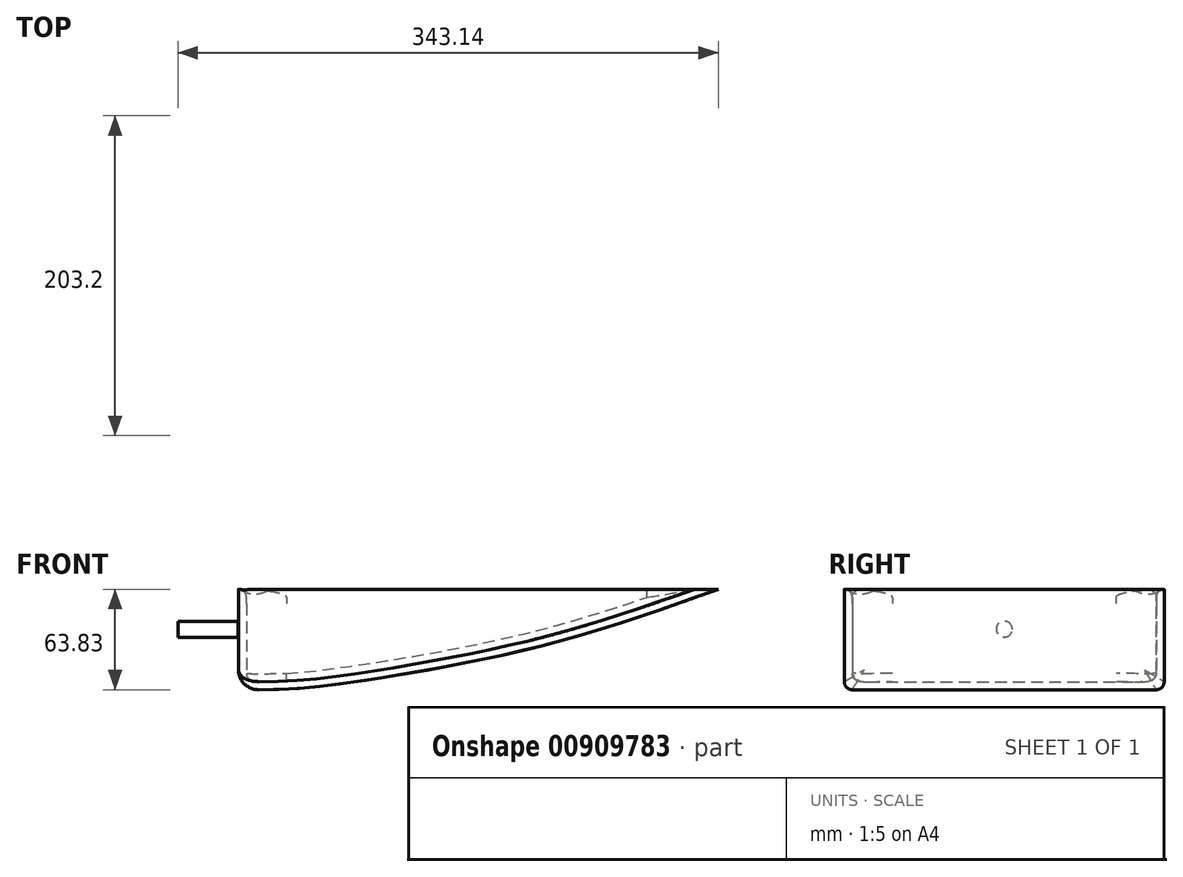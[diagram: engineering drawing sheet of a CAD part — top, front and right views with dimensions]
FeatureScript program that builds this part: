
annotation { "Feature Type Name" : "Feature", "Feature Type Description" : "" }
export const myFeature = defineFeature(function(context is Context, id is Id, definition is map)
    precondition{}
    {
        {
            var Q0;
            Q0=qCreatedBy(makeId("Front.planeOp"),FACE);
            var sketch = newSketch(context, id + "F0", { "sketchPlane" : qUnion([Q0])});
            skLineSegment(sketch, "E0", {"start": v(-126.76, 0) * mm, "end": v(178.04, 0) * mm});
            skLineSegment(sketch, "E1", {"start": v(-126.76, 0) * mm, "end": v(-126.76, -63.5) * mm});
            skFitSpline(sketch, "E2", {"points": [v(-126.76, -63.5) * mm, v(-96.17, -63.5) * mm, v(-41.35, -57.1) * mm, v(69.17, -35.07) * mm, v(178.04, 0) * mm], "startDerivative": vector(180.45, -5.15) * mm, "endDerivative": vector(339.41, 120.82) * mm});
            skSolve(sketch);
        }
        {
            var Q0;
            Q0 = qSketchRegion(id + "F0", true);
            extrude(context, id + "F1", {"entities" : qUnion([Q0]), "depth" : 203.2 * mm, "offsetDistance" : 25.4 * mm});
        }
        {
            var Q0;
            Q0=makeQuery(id+"F1.opExtrude","SWEPT_FACE",FACE,{"disambiguationData":[OSD([sQuery(id+"F0.wireOp",EDGE,"E0")])]});
            shell(context, id + "F2", {"entities" : qUnion([Q0]), "thickness" : 5.08 * mm});
        }
        {
            var Q0;
            {var subQ0=sQuery(id+"F0.wireOp",EDGE,"E2");Q0=makeQuery(id+"F2.opShell","OFFSET_EDGE",EDGE,{"disambiguationData":[OSD([subQ0]),TDD([makeQuery(id+"F1.opExtrude","CAP_EDGE",EDGE,{"disambiguationData":[OSD([subQ0])],"isStart":false})])]});}
            var Q1;
            {var subQ0=sQuery(id+"F0.wireOp",EDGE,"E2");Q1=makeQuery(id+"F2.opShell","OFFSET_EDGE",EDGE,{"disambiguationData":[OSD([subQ0]),TDD([makeQuery(id+"F1.opExtrude","CAP_EDGE",EDGE,{"disambiguationData":[OSD([subQ0])],"isStart":true})])]});}
            var Q2;
            Q2=makeQuery(id+"F1.opExtrude","CAP_EDGE",EDGE,{"disambiguationData":[OSD([sQuery(id+"F0.wireOp",EDGE,"E2")])],"isStart":true});
            var Q3;
            Q3=makeQuery(id+"F1.opExtrude","CAP_EDGE",EDGE,{"disambiguationData":[OSD([sQuery(id+"F0.wireOp",EDGE,"E2")])],"isStart":false});
            var Q4;
            {var subQ0=sQuery(id+"F0.wireOp",EDGE,"E0");Q4=makeQuery(id+"F2.opShell","OFFSET_EDGE",EDGE,{"disambiguationData":[OSD([subQ0]),TDD([makeQuery(id+"F1.opExtrude","CAP_EDGE",EDGE,{"disambiguationData":[OSD([subQ0])],"isStart":false})])]});}
            var Q5;
            Q5=makeQuery(id+"F2.opShell","OFFSET_EDGE",EDGE,{"disambiguationData":[OSD([sQuery(id+"F0.wireOp",EDGE,"E0"),sQuery(id+"F0.wireOp",EDGE,"E1")])]});
            var Q6;
            {var subQ0=sQuery(id+"F0.wireOp",EDGE,"E0");Q6=makeQuery(id+"F2.opShell","OFFSET_EDGE",EDGE,{"disambiguationData":[OSD([subQ0]),TDD([makeQuery(id+"F1.opExtrude","CAP_EDGE",EDGE,{"disambiguationData":[OSD([subQ0])],"isStart":true})])]});}
            var Q7;
            Q7=makeQuery(id+"F2.opShell","OFFSET_EDGE",EDGE,{"disambiguationData":[OSD([sQuery(id+"F0.wireOp",EDGE,"E1"),sQuery(id+"F0.wireOp",EDGE,"E2")])]});
            fillet(context, id + "F3", {"entities" : qUnion([Q0, Q1, Q2, Q3, Q4, Q5, Q6, Q7]), "radius" : 5.08 * mm, "tangentPropagation" : true, "allowEdgeOverflow" : false});
        }
        {
            var Q0;
            Q0=makeQuery(id+"F1.opExtrude","SWEPT_EDGE",EDGE,{"disambiguationData":[OSD([sQuery(id+"F0.wireOp",EDGE,"E1"),sQuery(id+"F0.wireOp",EDGE,"E2")])]});
            fillet(context, id + "F4", {"entities" : qUnion([Q0]), "radius" : 12.7 * mm, "tangentPropagation" : true, "allowEdgeOverflow" : false});
        }
        {
            var Q0;
            Q0=qCreatedBy(makeId("Right.planeOp"),FACE);
            cPlane(context, id + "F5", {"entities" : qUnion([Q0]), "cplaneType" : CPlaneType.OFFSET, "offset" : 127 * mm, "oppositeDirection" : true, "width" : 152.4 * mm, "height" : 152.4 * mm});
        }
        {
            var Q0;
            Q0=qCreatedBy(id+"F5.planeOp",FACE);
            var sketch = newSketch(context, id + "F6", { "sketchPlane" : qUnion([Q0])});
            skLineSegment(sketch, "E3", {"start": v(0, 0) * mm, "end": v(-203.2, 0) * mm});
            skLineSegment(sketch, "E4", {"start": v(0, 0) * mm, "end": v(-101.6, 0) * mm});
            skLineSegment(sketch, "E5", {"start": v(-101.6, 0) * mm, "end": v(-101.6, -25.4) * mm});
            skCircle(sketch, "E6", {"center": v(-101.6, -25.4) * mm, "radius": 5.08 * mm});
            skSolve(sketch);
        }
        {
            var Q0;
            Q0=makeQuery(id+"F6.imprint","IMPRINT",FACE,{"disambiguationData":[TD([[makeQuery(id+"F6.imprint","IMPRINT",EDGE,{"derivedFrom":sQuery(id+"F6.wireOp",EDGE,"E6")}),1.0]])]});
            extrude(context, id + "F7", {"entities" : qUnion([Q0]), "operationType" : NewBodyOperationType.ADD, "oppositeDirection" : true, "depth" : 38.1 * mm, "offsetDistance" : 25.4 * mm});
        }
        {
            var Q0;
            {var subQ0=sQuery(id+"F0.wireOp",EDGE,"E1");Q0=makeQuery(id+"F2.opShell","OFFSET_EDGE",EDGE,{"disambiguationData":[OSD([subQ0]),TDD([makeQuery(id+"F1.opExtrude","CAP_EDGE",EDGE,{"disambiguationData":[OSD([subQ0])],"isStart":true})])]});}
            var Q1;
            {var subQ0=sQuery(id+"F0.wireOp",EDGE,"E1");Q1=makeQuery(id+"F2.opShell","OFFSET_EDGE",EDGE,{"disambiguationData":[OSD([subQ0]),TDD([makeQuery(id+"F1.opExtrude","CAP_EDGE",EDGE,{"disambiguationData":[OSD([subQ0])],"isStart":false})])]});}
            fillet(context, id + "F8", {"entities" : qUnion([Q0, Q1]), "radius" : 25.4 * mm, "tangentPropagation" : true, "allowEdgeOverflow" : false});
        }
    });
